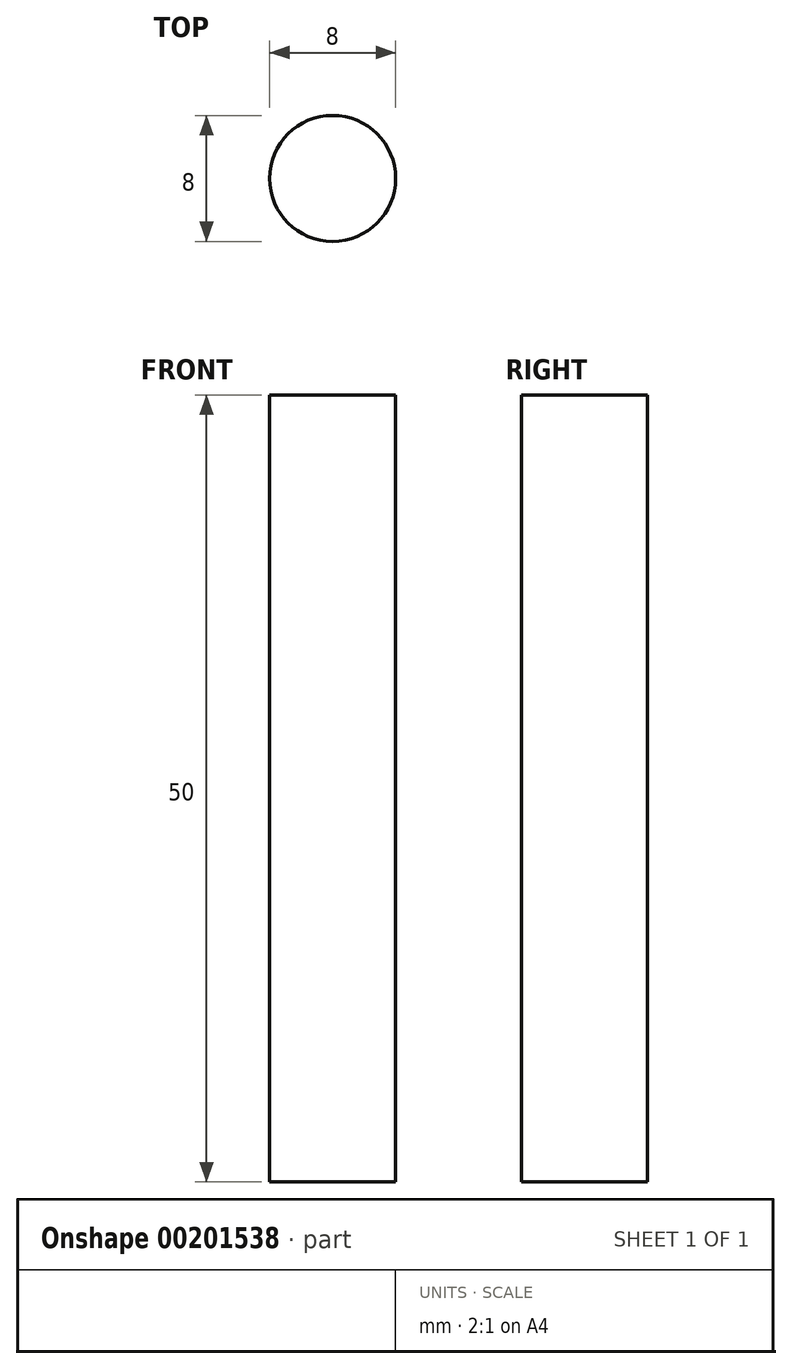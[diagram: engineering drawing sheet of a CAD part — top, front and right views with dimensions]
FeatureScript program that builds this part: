
annotation { "Feature Type Name" : "Feature", "Feature Type Description" : "" }
export const myFeature = defineFeature(function(context is Context, id is Id, definition is map)
    precondition{}
    {
        {
            var Q0;
            Q0=qCreatedBy(makeId("Top.planeOp"),FACE);
            var sketch = newSketch(context, id + "F0", { "sketchPlane" : qUnion([Q0])});
            skCircle(sketch, "E0", {"center": v(0, 0) * mm, "radius": 4 * mm});
            skSolve(sketch);
        }
        {
            var Q0;
            Q0 = qSketchRegion(id + "F0", true);
            extrude(context, id + "F1", {"entities" : qUnion([Q0]), "depth" : 50 * mm});
        }
    });
